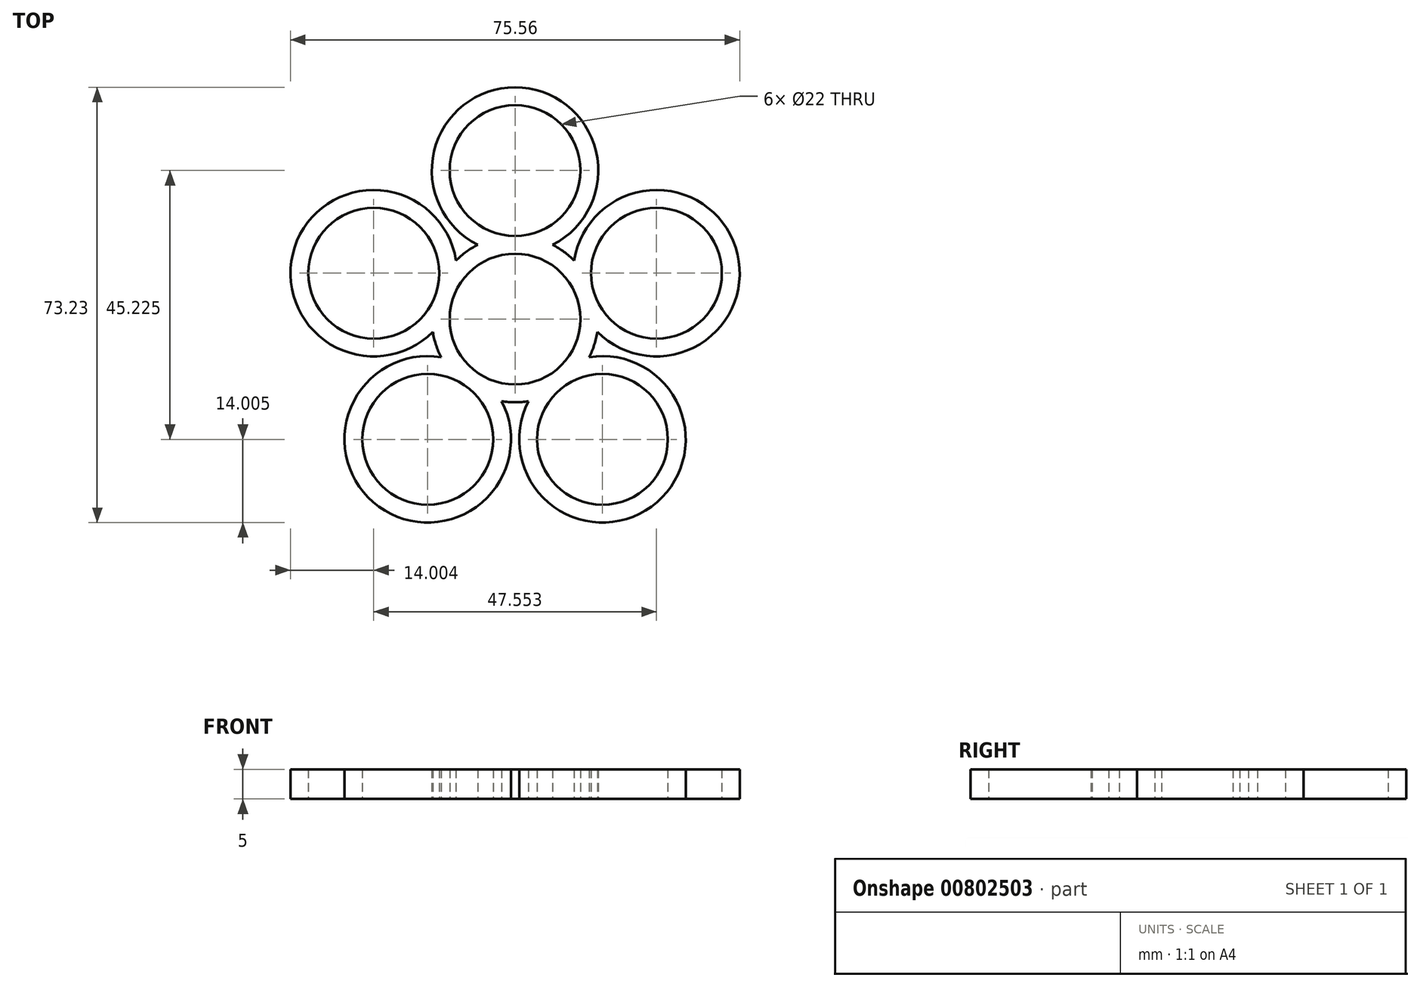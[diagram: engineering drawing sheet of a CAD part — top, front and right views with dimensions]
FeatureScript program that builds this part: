
annotation { "Feature Type Name" : "Feature", "Feature Type Description" : "" }
export const myFeature = defineFeature(function(context is Context, id is Id, definition is map)
    precondition{}
    {
        {
            var Q0;
            Q0=qCreatedBy(makeId("Top.planeOp"),FACE);
            var sketch = newSketch(context, id + "F0", { "sketchPlane" : qUnion([Q0])});
            skArc(sketch, "E0", {"start": v(6.47, 8.9) * mm, "mid": v(0, 11) * mm, "end": v(-6.47, 8.9) * mm});
            skCircle(sketch, "E1", {"center": v(0, 25) * mm, "radius": 11 * mm});
            skArc(sketch, "E2", {"start": v(6.3, 12.5) * mm, "mid": v(0, 39) * mm, "end": v(-6.3, 12.5) * mm});
            skArc(sketch, "E3", {"start": v(-6.3, 12.5) * mm, "mid": v(-7.3, 11.95) * mm, "end": v(-8.23, 11.33) * mm});
            skArc(sketch, "E4.trimOffspring", {"start": v(8.23, 11.33) * mm, "mid": v(7.3, 11.95) * mm, "end": v(6.3, 12.5) * mm});
            skArc(sketch, "E5.1.0", {"start": v(-9.94, 9.86) * mm, "mid": v(-37.1, 12.05) * mm, "end": v(-13.84, -2.13) * mm});
            skCircle(sketch, "E5.1.1", {"center": v(-23.78, 7.73) * mm, "radius": 11 * mm});
            skArc(sketch, "E5.1.2", {"start": v(-6.47, 8.9) * mm, "mid": v(-10.46, 3.4) * mm, "end": v(-10.46, -3.4) * mm});
            skArc(sketch, "E5.1.3", {"start": v(-8.23, 11.33) * mm, "mid": v(-9.11, 10.63) * mm, "end": v(-9.94, 9.86) * mm});
            skArc(sketch, "E5.1.4", {"start": v(-13.84, -2.13) * mm, "mid": v(-13.62, -3.24) * mm, "end": v(-13.31, -4.33) * mm});
            skArc(sketch, "E5.2.0", {"start": v(-12.45, -6.4) * mm, "mid": v(-22.92, -31.55) * mm, "end": v(-2.25, -13.82) * mm});
            skCircle(sketch, "E5.2.1", {"center": v(-14.7, -20.23) * mm, "radius": 11 * mm});
            skArc(sketch, "E5.2.2", {"start": v(-10.46, -3.4) * mm, "mid": v(-6.47, -8.9) * mm, "end": v(0, -11) * mm});
            skArc(sketch, "E5.2.3", {"start": v(-13.31, -4.33) * mm, "mid": v(-12.92, -5.38) * mm, "end": v(-12.45, -6.4) * mm});
            skArc(sketch, "E5.2.4", {"start": v(-2.25, -13.82) * mm, "mid": v(-1.13, -13.95) * mm, "end": v(0, -14) * mm});
            skArc(sketch, "E5.3.0", {"start": v(2.25, -13.82) * mm, "mid": v(22.92, -31.55) * mm, "end": v(12.45, -6.4) * mm});
            skCircle(sketch, "E5.3.1", {"center": v(14.7, -20.23) * mm, "radius": 11 * mm});
            skArc(sketch, "E5.3.2", {"start": v(0, -11) * mm, "mid": v(6.47, -8.9) * mm, "end": v(10.46, -3.4) * mm});
            skArc(sketch, "E5.3.3", {"start": v(0, -14) * mm, "mid": v(1.13, -13.95) * mm, "end": v(2.25, -13.82) * mm});
            skArc(sketch, "E5.3.4", {"start": v(12.45, -6.4) * mm, "mid": v(12.92, -5.38) * mm, "end": v(13.31, -4.33) * mm});
            skArc(sketch, "E5.4.0", {"start": v(13.84, -2.13) * mm, "mid": v(37.1, 12.05) * mm, "end": v(9.94, 9.86) * mm});
            skCircle(sketch, "E5.4.1", {"center": v(23.78, 7.73) * mm, "radius": 11 * mm});
            skArc(sketch, "E5.4.2", {"start": v(10.46, -3.4) * mm, "mid": v(10.46, 3.4) * mm, "end": v(6.47, 8.9) * mm});
            skArc(sketch, "E5.4.3", {"start": v(13.31, -4.33) * mm, "mid": v(13.62, -3.24) * mm, "end": v(13.84, -2.13) * mm});
            skArc(sketch, "E5.4.4", {"start": v(9.94, 9.86) * mm, "mid": v(9.11, 10.63) * mm, "end": v(8.23, 11.33) * mm});
            skSolve(sketch);
        }
        {
            var Q0;
            Q0 = qSketchRegion(id + "F0", true);
            extrude(context, id + "F1", {"entities" : qUnion([Q0]), "depth" : 5 * mm, "offsetDistance" : 25 * mm});
        }
    });
